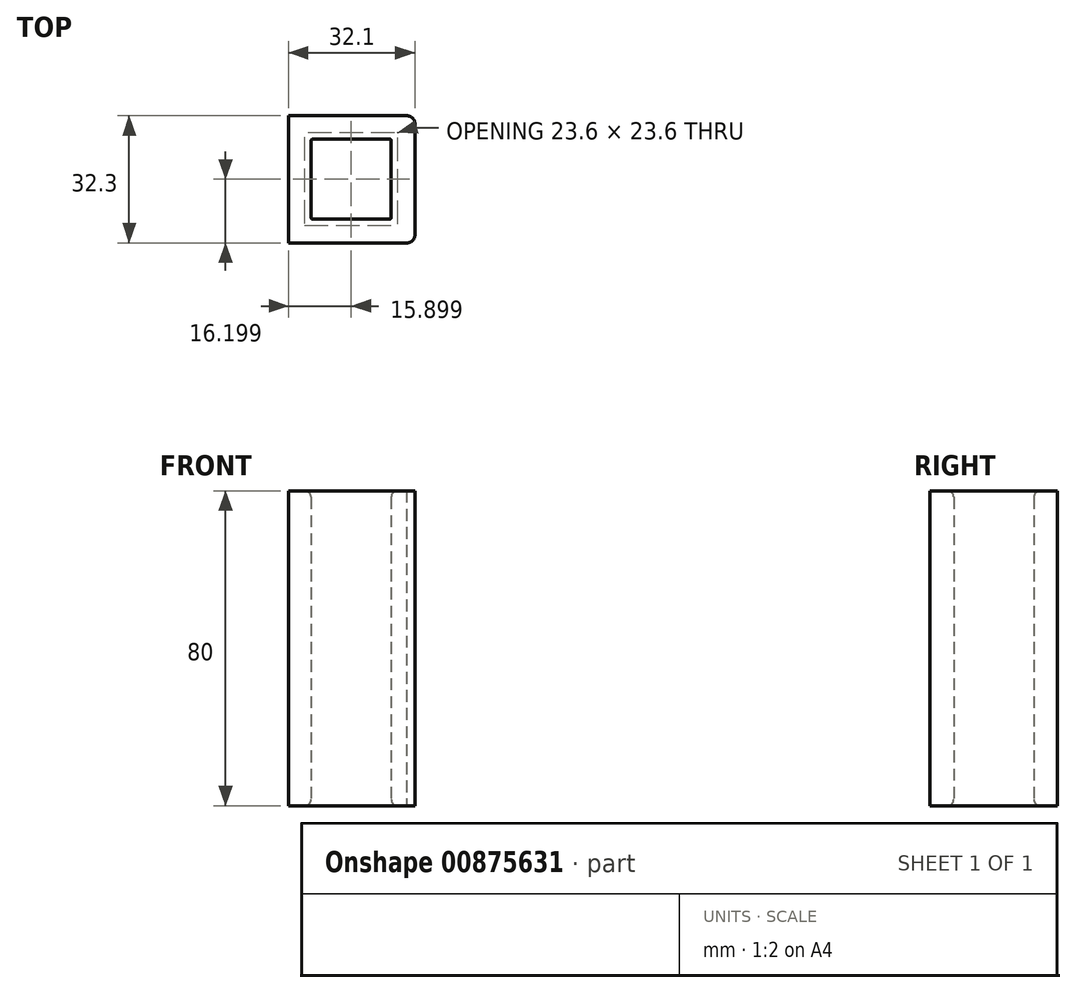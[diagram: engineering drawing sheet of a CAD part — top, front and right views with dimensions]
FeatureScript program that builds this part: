
annotation { "Feature Type Name" : "Feature", "Feature Type Description" : "" }
export const myFeature = defineFeature(function(context is Context, id is Id, definition is map)
    precondition{}
    {
        {
            var Q0;
            Q0=qCreatedBy(makeId("Top.planeOp"),FACE);
            var sketch = newSketch(context, id + "F0", { "sketchPlane" : qUnion([Q0])});
            skLineSegment(sketch, "E0.bottom", {"start": v(-49.08, 21.55) * mm, "end": v(-29.68, 21.55) * mm});
            skLineSegment(sketch, "E0.top", {"start": v(-49.08, 1.15) * mm, "end": v(-29.68, 1.15) * mm});
            skLineSegment(sketch, "E0.left", {"start": v(-49.58, 21.05) * mm, "end": v(-49.58, 1.65) * mm});
            skLineSegment(sketch, "E0.right", {"start": v(-29.18, 21.05) * mm, "end": v(-29.18, 1.65) * mm});
            skLineSegment(sketch, "E1.0", {"start": v(-23.18, 25.45) * mm, "end": v(-23.18, -2.85) * mm});
            skPoint(sketch, "E2.visualSharp", {"position": v(-49.58, 21.55) * mm});
            skArc(sketch, "E2.filletArc", {"start": v(-49.08, 21.55) * mm, "mid": v(-49.43, 21.4) * mm, "end": v(-49.58, 21.05) * mm});
            skPoint(sketch, "E3.visualSharp", {"position": v(-29.18, 21.55) * mm});
            skArc(sketch, "E3.filletArc", {"start": v(-29.18, 21.05) * mm, "mid": v(-29.33, 21.4) * mm, "end": v(-29.68, 21.55) * mm});
            skPoint(sketch, "E4.visualSharp", {"position": v(-29.18, 1.15) * mm});
            skArc(sketch, "E4.filletArc", {"start": v(-29.68, 1.15) * mm, "mid": v(-29.33, 1.3) * mm, "end": v(-29.18, 1.65) * mm});
            skPoint(sketch, "E5.visualSharp", {"position": v(-49.58, 1.15) * mm});
            skArc(sketch, "E5.filletArc", {"start": v(-49.58, 1.65) * mm, "mid": v(-49.43, 1.3) * mm, "end": v(-49.08, 1.15) * mm});
            skPoint(sketch, "E6.visualSharp", {"position": v(-23.18, 27.45) * mm});
            skArc(sketch, "E6.filletArc", {"start": v(-23.18, 25.45) * mm, "mid": v(-23.8, 26.9) * mm, "end": v(-25.28, 27.45) * mm});
            skPoint(sketch, "E7.visualSharp", {"position": v(-23.18, -4.85) * mm});
            skArc(sketch, "E7.filletArc", {"start": v(-25.18, -4.85) * mm, "mid": v(-23.77, -4.27) * mm, "end": v(-23.18, -2.85) * mm});
            skLineSegment(sketch, "E8", {"start": v(-25.28, 27.45) * mm, "end": v(-55.28, 27.45) * mm});
            skLineSegment(sketch, "E9", {"start": v(-25.18, -4.85) * mm, "end": v(-55.28, -4.85) * mm});
            skLineSegment(sketch, "E10", {"start": v(-55.28, 27.45) * mm, "end": v(-55.28, -4.85) * mm});
            skSolve(sketch);
        }
        {
            var Q0;
            Q0=makeQuery(id+"F0.imprint","IMPRINT",FACE,{"disambiguationData":[TD([[makeQuery(id+"F0.imprint","IMPRINT",EDGE,{"derivedFrom":sQuery(id+"F0.wireOp",EDGE,"E0.bottom")}),1.0]])]});
            extrude(context, id + "F1", {"entities" : qUnion([Q0]), "depth" : 80 * mm, "offsetDistance" : 25 * mm});
        }
        {
            var Q0;
            Q0=makeQuery(id+"F1.opExtrude","CAP_EDGE",EDGE,{"disambiguationData":[OSD([sQuery(id+"F0.wireOp",EDGE,"E0.bottom")])],"isStart":true});
            var Q1;
            Q1=makeQuery(id+"F1.opExtrude","CAP_EDGE",EDGE,{"disambiguationData":[OSD([sQuery(id+"F0.wireOp",EDGE,"E0.bottom")])],"isStart":false});
            fillet(context, id + "F2", {"entities" : qUnion([Q0, Q1]), "radius" : 1.6 * mm, "tangentPropagation" : true, "allowEdgeOverflow" : false});
        }
    });
